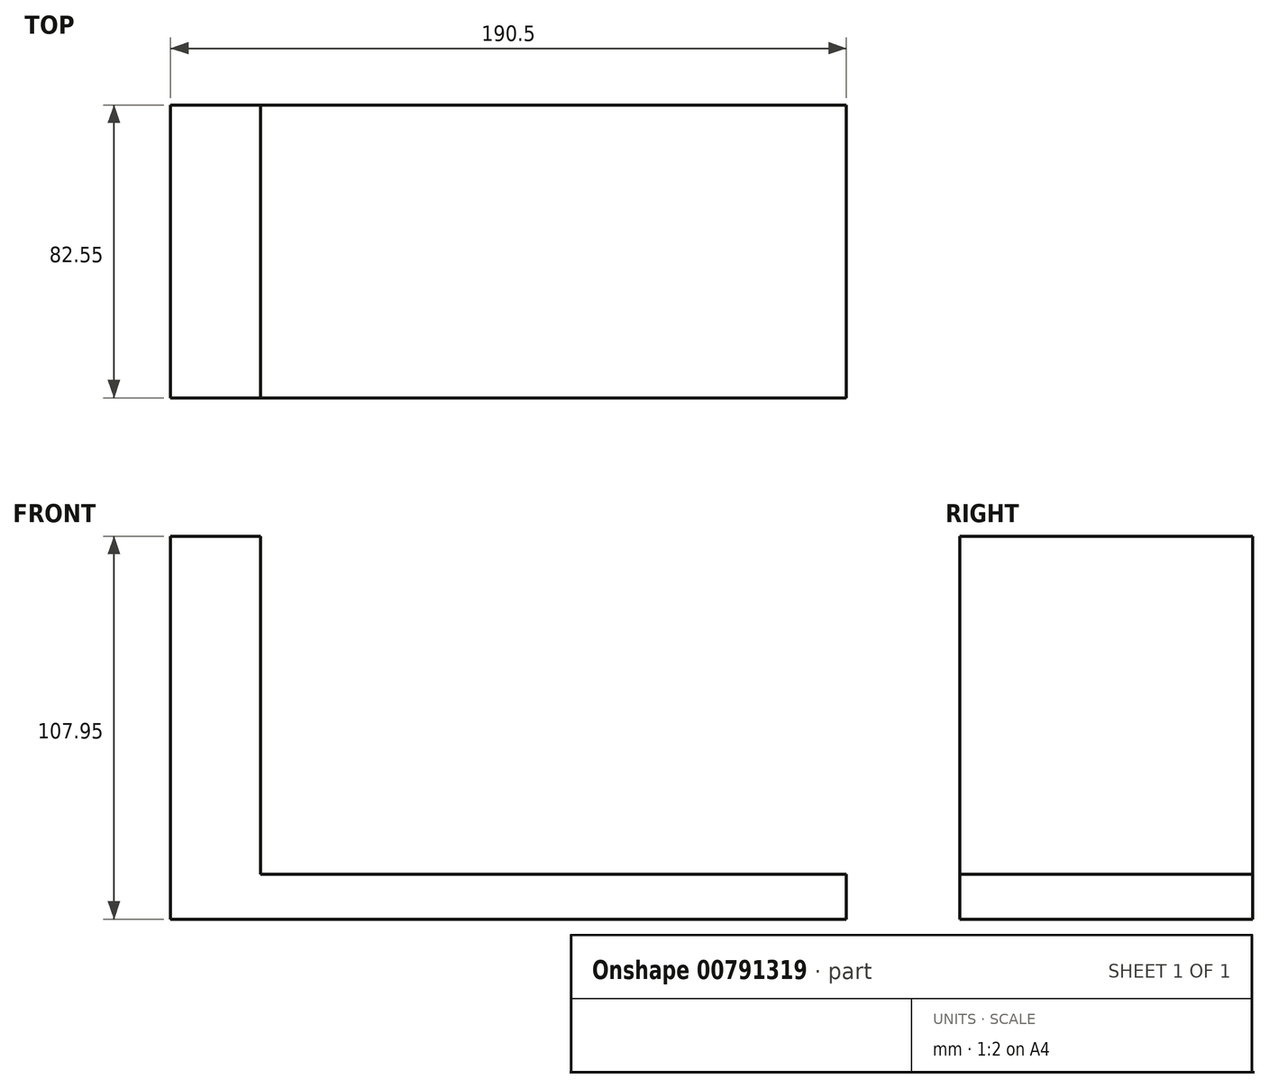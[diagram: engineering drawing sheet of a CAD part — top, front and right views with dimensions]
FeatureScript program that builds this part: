
annotation { "Feature Type Name" : "Feature", "Feature Type Description" : "" }
export const myFeature = defineFeature(function(context is Context, id is Id, definition is map)
    precondition{}
    {
        {
            var Q0;
            Q0=qCreatedBy(makeId("Front.planeOp"),FACE);
            var sketch = newSketch(context, id + "F0", { "sketchPlane" : qUnion([Q0])});
            skLineSegment(sketch, "E0", {"start": v(0, 0) * mm, "end": v(190.5, 0) * mm});
            skLineSegment(sketch, "E1", {"start": v(0, 0) * mm, "end": v(0, 107.95) * mm});
            skLineSegment(sketch, "E2", {"start": v(190.5, 0) * mm, "end": v(190.5, 12.7) * mm});
            skLineSegment(sketch, "E3", {"start": v(190.5, 12.7) * mm, "end": v(25.4, 12.7) * mm});
            skLineSegment(sketch, "E4", {"start": v(0, 107.95) * mm, "end": v(25.4, 107.95) * mm});
            skLineSegment(sketch, "E5", {"start": v(25.4, 107.95) * mm, "end": v(25.4, 12.7) * mm});
            skSolve(sketch);
        }
        {
            var Q0;
            Q0=makeQuery(id+"F0.imprint","IMPRINT",FACE,{"disambiguationData":[TD([[makeQuery(id+"F0.imprint","IMPRINT",EDGE,{"derivedFrom":sQuery(id+"F0.wireOp",EDGE,"E0")}),1.0]])]});
            extrude(context, id + "F1", {"entities" : qUnion([Q0]), "depth" : 82.55 * mm, "offsetDistance" : 25.4 * mm});
        }
    });
